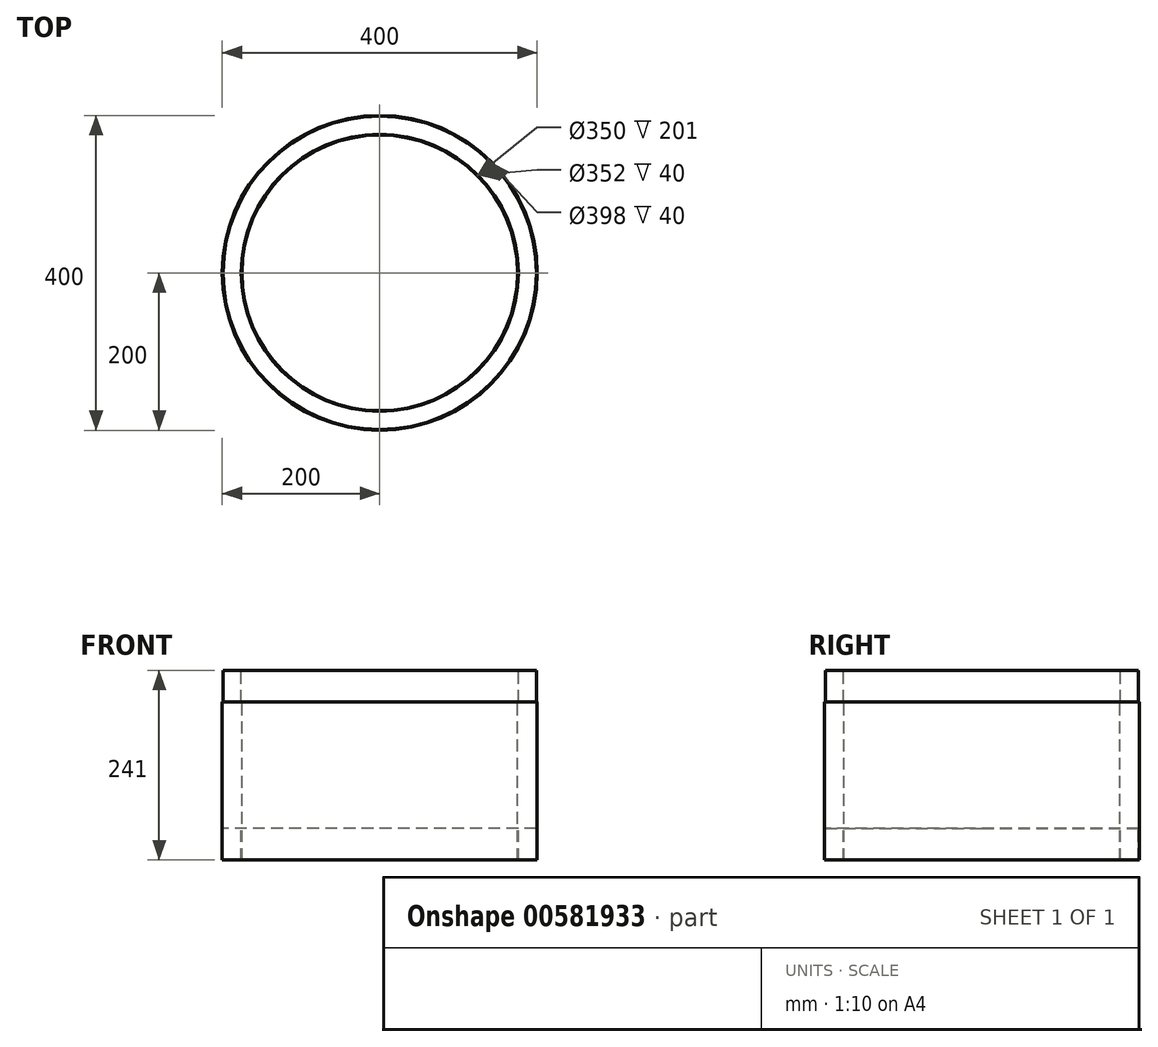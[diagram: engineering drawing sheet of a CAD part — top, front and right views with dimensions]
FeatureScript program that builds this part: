
annotation { "Feature Type Name" : "Feature", "Feature Type Description" : "" }
export const myFeature = defineFeature(function(context is Context, id is Id, definition is map)
    precondition{}
    {
        {
            var Q0;
            Q0=qCreatedBy(makeId("Front.planeOp"),FACE);
            var sketch = newSketch(context, id + "F0", { "sketchPlane" : qUnion([Q0])});
            skLineSegment(sketch, "E0", {"start": v(0, 345.75) * mm, "end": v(0, -558.03) * mm, "construction": true});
            skLineSegment(sketch, "E1", {"start": v(-175, -518.84) * mm, "end": v(-175, -317.84) * mm});
            skLineSegment(sketch, "E2", {"start": v(-175, -317.84) * mm, "end": v(-176, -317.84) * mm});
            skLineSegment(sketch, "E3", {"start": v(-176, -317.84) * mm, "end": v(-176, -277.84) * mm});
            skLineSegment(sketch, "E4", {"start": v(-176, -277.84) * mm, "end": v(-199, -277.84) * mm});
            skLineSegment(sketch, "E5", {"start": v(-199, -277.84) * mm, "end": v(-199, -317.84) * mm});
            skLineSegment(sketch, "E6", {"start": v(-199, -317.84) * mm, "end": v(-200, -317.84) * mm});
            skLineSegment(sketch, "E7", {"start": v(-200, -317.84) * mm, "end": v(-200, -518.84) * mm});
            skLineSegment(sketch, "E8", {"start": v(-200, -518.84) * mm, "end": v(-199, -518.84) * mm});
            skLineSegment(sketch, "E9", {"start": v(-199, -518.84) * mm, "end": v(-199, -478.84) * mm});
            skLineSegment(sketch, "E10", {"start": v(-199, -478.84) * mm, "end": v(-176, -478.84) * mm});
            skLineSegment(sketch, "E11", {"start": v(-176, -478.84) * mm, "end": v(-176, -518.84) * mm});
            skLineSegment(sketch, "E12", {"start": v(-176, -518.84) * mm, "end": v(-175, -518.84) * mm});
            skSolve(sketch);
        }
        {
            var Q0;
            Q0=qSketchRegion(id+"F0",true);
            var Q1;
            Q1=sQuery(id+"F0.wireOp",EDGE,"E0");
            revolve(context, id + "F1", {"entities" : qUnion([Q0]), "axis" : qUnion([Q1]), "revolveType" : RevolveType.FULL});
        }
    });
